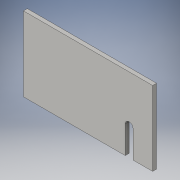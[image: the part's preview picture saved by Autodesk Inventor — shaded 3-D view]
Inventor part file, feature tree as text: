
AUTODESK INVENTOR PART (.ipt)
format: ipt  version: 2016 (Build 200138000, 138)  size: 98,304 bytes
history: native  units: in
note: dims shown in document units (in); Inventor stores cm internally (conversion verified against a paired STEP export)
features: extrude x1, sketch x1
ambient origin geometry x8: Origin, YZ Plane, XZ Plane, XY Plane, X Axis, Y Axis, Z Axis, Center Point
bodies: Solid1 (feature_tree)
feature tree (2):
  extrude  "Extrusion1"  Depth=9.5in
  sketch  "Sketch1"  dims[d0=16.5in d1=9.5in d2=1.0in d3=3.0in d4=3.5in d5=3.5in d6=0.5in d7=0.0in]
